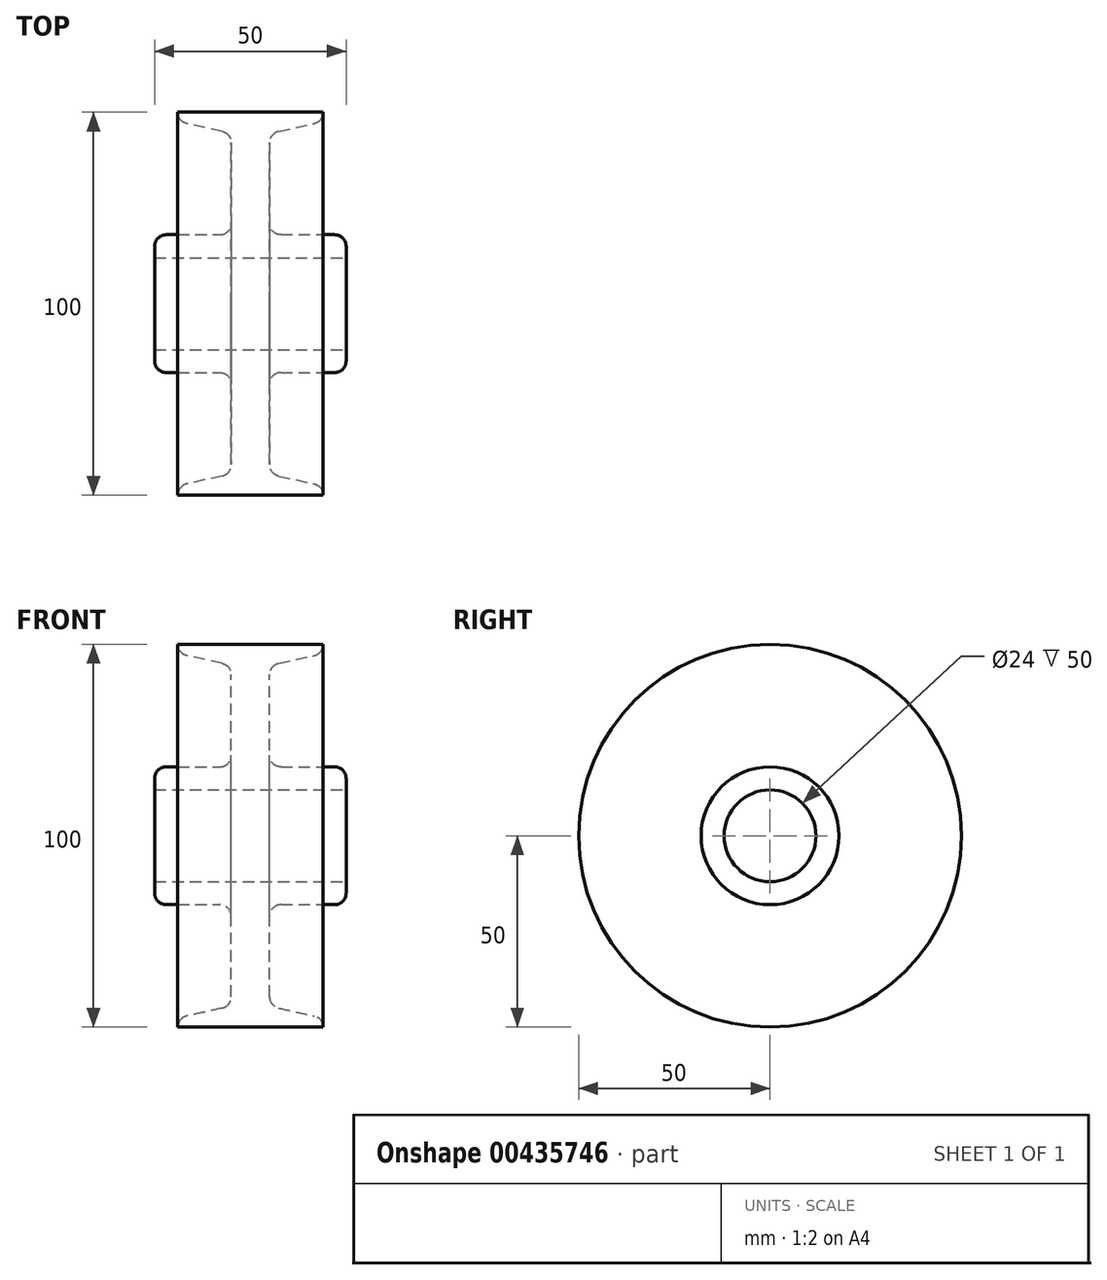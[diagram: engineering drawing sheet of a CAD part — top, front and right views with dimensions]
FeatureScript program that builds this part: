
annotation { "Feature Type Name" : "Feature", "Feature Type Description" : "" }
export const myFeature = defineFeature(function(context is Context, id is Id, definition is map)
    precondition{}
    {
        {
            var Q0;
            Q0=qCreatedBy(makeId("Top.planeOp"),FACE);
            var sketch = newSketch(context, id + "F0", { "sketchPlane" : qUnion([Q0])});
            skLineSegment(sketch, "E0", {"start": v(0, 0) * mm, "end": v(-33.68, 0) * mm, "construction": true});
            skLineSegment(sketch, "E1.0", {"start": v(-8, -18) * mm, "end": v(-22, -18) * mm});
            skLineSegment(sketch, "E2.0", {"start": v(-5, -21) * mm, "end": v(-5, -42.07) * mm});
            skLineSegment(sketch, "E3", {"start": v(-16.65, -47.07) * mm, "end": v(-7.35, -45) * mm});
            skLineSegment(sketch, "E4.0", {"start": v(-25, -12) * mm, "end": v(-25, -15) * mm});
            skPoint(sketch, "E5.visualSharp", {"position": v(-5, -18) * mm});
            skArc(sketch, "E5.filletArc", {"start": v(-5, -21) * mm, "mid": v(-5.88, -18.88) * mm, "end": v(-8, -18) * mm});
            skPoint(sketch, "E6.visualSharp", {"position": v(-5, -44.48) * mm});
            skArc(sketch, "E6.filletArc", {"start": v(-7.35, -45) * mm, "mid": v(-5.66, -43.95) * mm, "end": v(-5, -42.07) * mm});
            skPoint(sketch, "E7.visualSharp", {"position": v(-25, -18) * mm});
            skArc(sketch, "E7.filletArc", {"start": v(-25, -15) * mm, "mid": v(-24.12, -17.12) * mm, "end": v(-22, -18) * mm});
            skArc(sketch, "E8", {"start": v(-16.65, -47.07) * mm, "mid": v(-18.34, -48.12) * mm, "end": v(-19, -50) * mm});
            skArc(sketch, "E9.MirrorCS", {"start": v(7.35, -45) * mm, "mid": v(5.66, -43.95) * mm, "end": v(5, -42.07) * mm});
            skArc(sketch, "E10.MirrorCS", {"start": v(5, -21) * mm, "mid": v(5.88, -18.88) * mm, "end": v(8, -18) * mm});
            skArc(sketch, "E11.MirrorCS", {"start": v(16.65, -47.07) * mm, "mid": v(18.34, -48.12) * mm, "end": v(19, -50) * mm});
            skPoint(sketch, "E12.MirrorP", {"position": v(5, -44.48) * mm});
            skLineSegment(sketch, "E13.MirrorCS", {"start": v(5, -21) * mm, "end": v(5, -42.07) * mm});
            skLineSegment(sketch, "E14.MirrorCS", {"start": v(16.65, -47.07) * mm, "end": v(7.35, -45) * mm});
            skLineSegment(sketch, "E15.MirrorCS", {"start": v(-25, -12) * mm, "end": v(25, -12) * mm});
            skLineSegment(sketch, "E16.MirrorCS", {"start": v(-19, -50) * mm, "end": v(19, -50) * mm});
            skLineSegment(sketch, "E17.MirrorCS", {"start": v(8, -18) * mm, "end": v(22, -18) * mm});
            skLineSegment(sketch, "E18.MirrorCS", {"start": v(25, -12) * mm, "end": v(25, -15) * mm});
            skPoint(sketch, "E19.MirrorP", {"position": v(5, -18) * mm});
            skArc(sketch, "E20.MirrorCS", {"start": v(25, -15) * mm, "mid": v(24.12, -17.12) * mm, "end": v(22, -18) * mm});
            skPoint(sketch, "E21.MirrorP", {"position": v(25, -18) * mm});
            skSolve(sketch);
        }
        {
            var Q0;
            Q0=makeQuery(id+"F0.imprint","IMPRINT",FACE,{"disambiguationData":[TD([[makeQuery(id+"F0.imprint","IMPRINT",EDGE,{"derivedFrom":sQuery(id+"F0.wireOp",EDGE,"E1.0")}),-1.0]])]});
            var Q1;
            Q1=sQuery(id+"F0.wireOp",EDGE,"E0");
            revolve(context, id + "F1", {"entities" : qUnion([Q0]), "axis" : qUnion([Q1]), "revolveType" : RevolveType.FULL});
        }
    });
